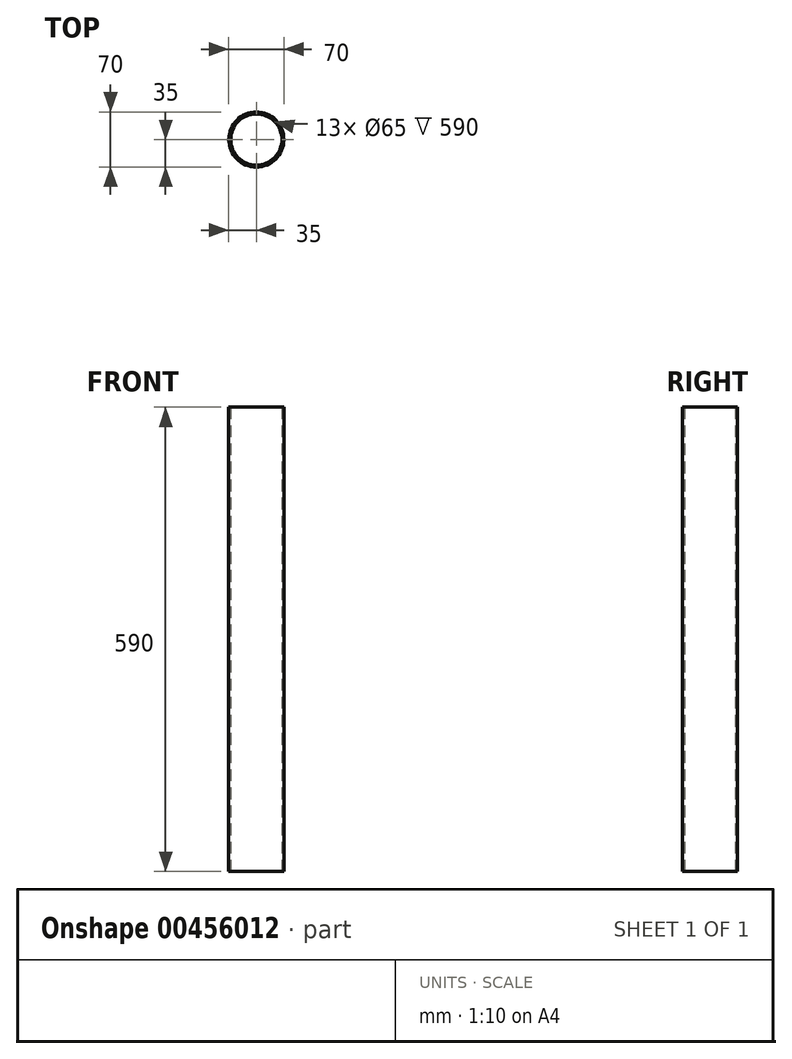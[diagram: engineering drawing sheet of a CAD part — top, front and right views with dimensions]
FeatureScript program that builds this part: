
annotation { "Feature Type Name" : "Feature", "Feature Type Description" : "" }
export const myFeature = defineFeature(function(context is Context, id is Id, definition is map)
    precondition{}
    {
        {
            var Q0;
            Q0=qCreatedBy(makeId("Top.planeOp"),FACE);
            var sketch = newSketch(context, id + "F0", { "sketchPlane" : qUnion([Q0])});
            skCircle(sketch, "E0", {"center": v(0, 0) * mm, "radius": 35 * mm});
            skCircle(sketch, "E1", {"center": v(0, 0) * mm, "radius": 32.5 * mm});
            skSolve(sketch);
        }
        {
            var Q0;
            Q0=makeQuery(id+"F0.imprint","IMPRINT",FACE,{"disambiguationData":[TD([[makeQuery(id+"F0.imprint","IMPRINT",EDGE,{"derivedFrom":sQuery(id+"F0.wireOp",EDGE,"E0")}),1.0]])]});
            extrude(context, id + "F1", {"entities" : qUnion([Q0]), "depth" : 590 * mm});
        }
    });
